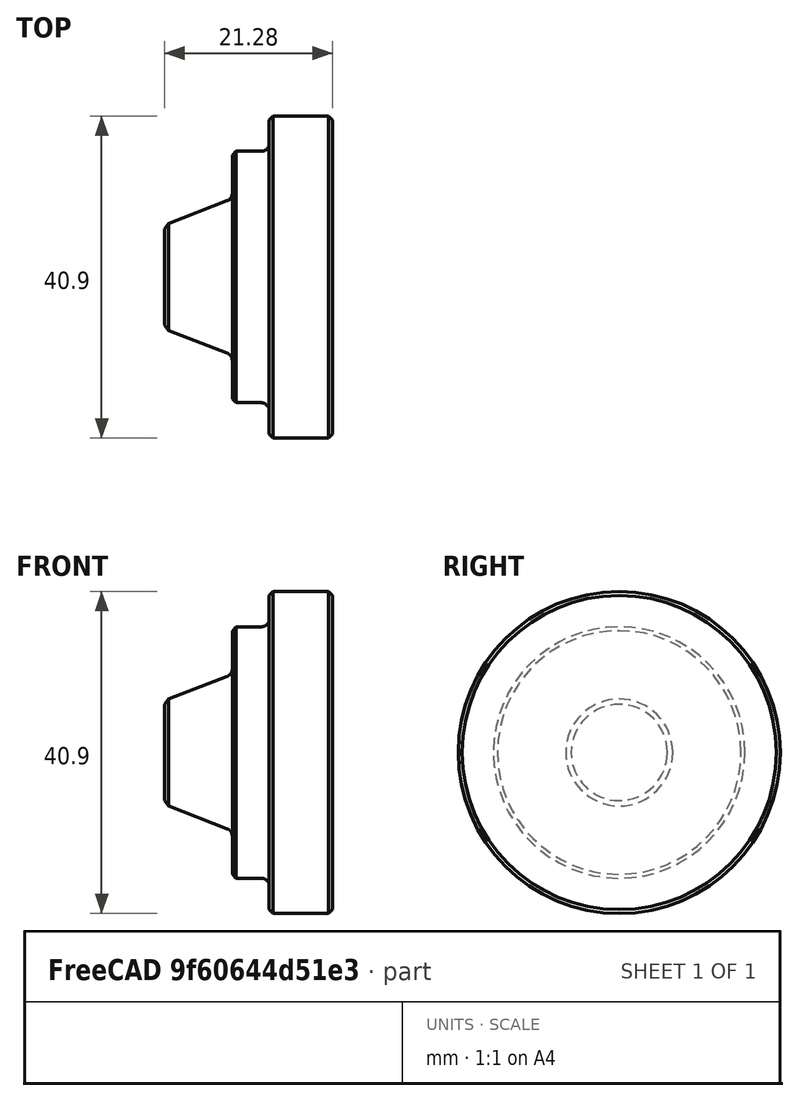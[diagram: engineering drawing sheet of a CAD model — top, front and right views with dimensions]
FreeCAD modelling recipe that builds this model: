
FCSTD DOCUMENT  (FreeCAD 0.19R24291 (Git))
Label: surface-roughness
License: All rights reserved
LicenseURL: http://en.wikipedia.org/wiki/All_rights_reserved
objects: TechDraw::DrawViewSymbol×16, TechDraw::DrawViewAnnotation×5, Sketcher::SketchObject×2, PartDesign::Revolution×2, PartDesign::Chamfer×2, PartDesign::Fillet×2, PartDesign::Body×2, TechDraw::DrawProjGroupItem×2, TechDraw::DrawSVGTemplate×1, TechDraw::DrawProjGroup×1, TechDraw::DrawViewBalloon×1, TechDraw::DrawPage×1
note: 16 computed .brp shape members not serialized (recipe doc carries the construction recipe); baked Part::Feature solids carry a one-line shape summary decoded from their .brp

FEATURE [Sketcher::SketchObject] Sketch
  FullyConstrained = true
  MapMode = 5
  Support = -> [XY_Plane]
  sketch-geometry (8):
    g0: LineSegment StartX=0 StartY=0 StartZ=0 EndX=0 EndY=6.61 EndZ=0
    g1: LineSegment StartX=0 StartY=6.61 StartZ=0 EndX=8.58 EndY=9.93 EndZ=0
    g2: LineSegment StartX=8.58 StartY=9.93 StartZ=0 EndX=8.58 EndY=15.97 EndZ=0
    g3: LineSegment StartX=8.58 StartY=15.97 StartZ=0 EndX=13.27 EndY=15.97 EndZ=0
    g4: LineSegment StartX=13.27 StartY=15.97 StartZ=0 EndX=13.27 EndY=20.45 EndZ=0
    g5: LineSegment StartX=13.27 StartY=20.45 StartZ=0 EndX=21.28 EndY=20.45 EndZ=0
    g6: LineSegment StartX=21.28 StartY=20.45 StartZ=0 EndX=21.28 EndY=0 EndZ=0
    g7: LineSegment StartX=21.28 StartY=0 StartZ=0 EndX=0 EndY=0 EndZ=0
  constraints (23):
    c: Coincident(g0,g-1)
    c: PointOnObject(g0,g-2)
    c: Coincident(g0,g1)
    c: Coincident(g1,g2)
    c: Vertical(g2)
    c: Coincident(g2,g3)
    c: Coincident(g3,g4)
    c: Vertical(g4)
    c: Coincident(g4,g5)
    c: Horizontal(g5)
    c: Coincident(g5,g6)
    c: PointOnObject(g6,g-1)
    c: Vertical(g6)
    c: Coincident(g6,g7)
    c: Coincident(g7,g0)
    c: Horizontal(g3)
    c: DistanceX(g5,g5) = 8.01
    c: DistanceY(g6,g6) = 20.45
    c: DistanceY(g0,g0) = 6.61
    c: DistanceY(g2,g2) = 6.04
    c: DistanceY(g4,g4) = 4.48
    c: DistanceX(g7,g7) = 21.28
    c: DistanceX(g3,g3) = 4.69
FEATURE [PartDesign::Revolution] Revolution
  Angle = 360
  Axis = (1,0,0)
  Base = (0,0,0)
  Profile = -> Sketch
  ReferenceAxis = -> X_Axis
  Reversed = true
FEATURE [PartDesign::Chamfer] Chamfer
  Angle = 45
  Base = -> Revolution [Edge1,Edge4,Edge7,Edge8]
  BaseFeature = -> Revolution
  ChamferType = 0
  FlipDirection = false
  Size = 0.5
  Size2 = 1
  SupportTransform = false
FEATURE [PartDesign::Fillet] Fillet
  Base = -> Chamfer [Edge5,Edge10]
  BaseFeature = -> Chamfer
  Radius = 1
  SupportTransform = false
FEATURE [PartDesign::Body] Body
  Group = -> [Sketch,Revolution,Chamfer,Fillet]
  Origin = -> Origin
  Tip = -> Fillet
FEATURE [TechDraw::DrawSVGTemplate] Template
  EditableTexts = Designed_by_Name=Designed by Name; Drawing_number=Drawing number; FC-Date=Date; FC-SC=Scale; FC-SH=Sheet; FC-Title=Title; Subtitle=Subtitle; Weight=Weight
  Height = 210
  Orientation = 1
  Width = 297
FEATURE [TechDraw::DrawProjGroupItem] ProjItem  label="Front"
  CoarseView = false
  Direction = (-1,0,0)
  Focus = 100
  HardHidden = false
  IsoCount = 0
  IsoHidden = false
  IsoVisible = false
  LockPosition = true
  Perspective = false
  Rotation = 0
  RotationVector = (0,-1,0)
  Scale = 2
  ScaleType = 2
  SeamHidden = false
  SeamVisible = true
  SmoothHidden = false
  SmoothVisible = true
  Source = -> [Body]
  Type = 0
  X = 0
  XDirection = (0,-1,0)
  Y = 0
FEATURE [TechDraw::DrawProjGroupItem] ProjItem001  label="Left"
  CoarseView = false
  Direction = (-1e-16,1,0)
  Focus = 100
  HardHidden = false
  IsoCount = 0
  IsoHidden = false
  IsoVisible = false
  LockPosition = false
  Perspective = false
  Rotation = 0
  RotationVector = (1,0,0)
  Scale = 2
  ScaleType = 2
  SeamHidden = false
  SeamVisible = true
  SmoothHidden = false
  SmoothVisible = true
  Source = -> [Body]
  Type = 1
  X = 77.18
  XDirection = (-1,-1e-16,0)
  Y = 0
FEATURE [TechDraw::DrawProjGroup] ProjGroup
  Anchor = -> ProjItem
  AutoDistribute = true
  LockPosition = false
  ProjectionType = 0
  Rotation = 0
  Scale = 2
  ScaleType = 2
  Source = -> [Body]
  Views = -> [ProjItem,ProjItem001]
  X = 86.8739
  Y = 132.576
  spacingX = 15
  spacingY = 15
FEATURE [TechDraw::DrawViewSymbol] Symbol
  LockPosition = false
  Rotation = 0
  ScaleType = 2
  Symbol = <?xml version="1.0" encoding="UTF-8" standalone="no"?>\n<!-- Created with Inkscape (http://www.inkscape.org/) -->\n\n<svg\n   width="24.9319mm"\n   height="10.867571mm"\n   viewBox="0 0 24.9319 10.867571"\n   version="1.1"\n   id="svg5"\n   inkscape:version="1.1.1 (3bf5ae0d25, 2021-09-20)"\n   sodipodi:docname="roughness.svg"\n   xmlns:inkscape="http://www.inkscape.org/namespaces/inkscape"\n   xmlns:sodipodi="http://sodipodi.sourceforge.net/DTD/sodipodi-0.dtd"\n   xmlns="http://www.w3.org/2000/svg"\n   xmlns:svg="http://www.w3.org/2000/svg">\n  <sodipodi:namedview\n     id="namedview7"\n     pagecolor="#ffffff"\n     bordercolor="#999999"\n     borderopacity="1"\n     inkscape:pageshadow="0"\n     inkscape:pageopacity="0"\n     inkscape:pagecheckerboard="0"\n     inkscape:document-units="mm"\n     showgrid="false"\n     inkscape:zoom="3.1108586"\n     inkscape:cx="78.113483"\n     inkscape:cy="5.6254566"\n     inkscape:window-width="1600"\n     inkscape:window-height="1137"\n     inkscape:window-x="-8"\n     inkscape:window-y="-8"\n     inkscape:window-maximized="1"\n     inkscape:current-layer="layer1"\n     showborder="true"\n     fit-margin-top="0"\n     fit-margin-left="0"\n     fit-margin-right="0"\n     fit-margin-bottom="0" />\n  <defs\n     id="defs2" />\n  <g\n     inkscape:label="Ebene 1"\n     inkscape:groupmode="layer"\n     id="layer1"\n     transform="translate(-13.037144,-40.097097)">\n    <path\n       style="fill:none;stroke:#000000;stroke-width:0.135895px;stroke-linecap:butt;stroke-linejoin:miter;stroke-opacity:1"\n       d="m 13.155737,45.756607 2.97052,5.067357 2.621047,-5.067357 z"\n       id="path42" />\n    <path\n       style="fill:none;stroke:#000000;stroke-width:0.135895px;stroke-linecap:butt;stroke-linejoin:miter;stroke-opacity:1"\n       d="m 18.747304,45.756607 2.970519,-5.41683 16.25049,-0.174736"\n       id="path44" />\n  </g>\n</svg>
  X = 203.662
  Y = 173.18
FEATURE [TechDraw::DrawViewAnnotation] Annotation
  Font = osifont
  LineSpace = 80
  LockPosition = false
  MaxWidth = -1
  Rotation = 0
  ScaleType = 0
  Text = Ra 6,3
  TextSize = 5
  TextStyle = 0
  X = 207.602
  Y = 173.223
FEATURE [TechDraw::DrawViewSymbol] Symbol001
  LockPosition = false
  Rotation = 0
  ScaleType = 2
  Symbol = <?xml version="1.0" encoding="UTF-8" standalone="no"?>\n<!-- Created with Inkscape (http://www.inkscape.org/) -->\n\n<svg\n   width="8.6807499mm"\n   height="10.655431mm"\n   viewBox="0 0 8.6807499 10.655431"\n   version="1.1"\n   id="svg5"\n   inkscape:version="1.1.1 (3bf5ae0d25, 2021-09-20)"\n   sodipodi:docname="roughness-1-1.svg"\n   xmlns:inkscape="http://www.inkscape.org/namespaces/inkscape"\n   xmlns:sodipodi="http://sodipodi.sourceforge.net/DTD/sodipodi-0.dtd"\n   xmlns="http://www.w3.org/2000/svg"\n   xmlns:svg="http://www.w3.org/2000/svg">\n  <sodipodi:namedview\n     id="namedview7"\n     pagecolor="#ffffff"\n     bordercolor="#999999"\n     borderopacity="1"\n     inkscape:pageshadow="0"\n     inkscape:pageopacity="0"\n     inkscape:pagecheckerboard="0"\n     inkscape:document-units="mm"\n     showgrid="false"\n     inkscape:zoom="8.7988368"\n     inkscape:cx="19.491213"\n     inkscape:cy="16.877231"\n     inkscape:window-width="1600"\n     inkscape:window-height="1137"\n     inkscape:window-x="-8"\n     inkscape:window-y="-8"\n     inkscape:window-maximized="1"\n     inkscape:current-layer="layer2"\n     showborder="true"\n     fit-margin-top="0"\n     fit-margin-left="0"\n     fit-margin-right="0"\n     fit-margin-bottom="0" />\n  <defs\n     id="defs2" />\n  <g\n     inkscape:groupmode="layer"\n     id="layer2"\n     inkscape:label="Ebene 2"\n     style="display:inline"\n     transform="translate(-0.05992954,-0.21068)">\n    <path\n       style="fill:none;stroke:#000000;stroke-width:0.136;stroke-linecap:butt;stroke-linejoin:miter;stroke-miterlimit:4;stroke-dasharray:none;stroke-opacity:1"\n       d="M 0.118593,5.6595099 3.089113,10.726867 8.680679,0.24268"\n       id="path1391" />\n  </g>\n</svg>
  X = 203.172
  Y = 151.04
FEATURE [TechDraw::DrawViewSymbol] Symbol002
  LockPosition = false
  Rotation = 0
  ScaleType = 2
  Symbol = <?xml version="1.0" encoding="UTF-8" standalone="no"?>\n<!-- Created with Inkscape (http://www.inkscape.org/) -->\n\n<svg\n   width="8.7402563mm"\n   height="10.657563mm"\n   viewBox="0 0 8.7402563 10.657563"\n   version="1.1"\n   id="svg5"\n   inkscape:version="1.1.1 (3bf5ae0d25, 2021-09-20)"\n   sodipodi:docname="roughness-1-2.svg"\n   xmlns:inkscape="http://www.inkscape.org/namespaces/inkscape"\n   xmlns:sodipodi="http://sodipodi.sourceforge.net/DTD/sodipodi-0.dtd"\n   xmlns="http://www.w3.org/2000/svg"\n   xmlns:svg="http://www.w3.org/2000/svg">\n  <sodipodi:namedview\n     id="namedview7"\n     pagecolor="#ffffff"\n     bordercolor="#999999"\n     borderopacity="1"\n     inkscape:pageshadow="0"\n     inkscape:pageopacity="0"\n     inkscape:pagecheckerboard="0"\n     inkscape:document-units="mm"\n     showgrid="false"\n     inkscape:zoom="6.2217172"\n     inkscape:cx="43.63747"\n     inkscape:cy="16.153097"\n     inkscape:window-width="1600"\n     inkscape:window-height="1137"\n     inkscape:window-x="-8"\n     inkscape:window-y="-8"\n     inkscape:window-maximized="1"\n     inkscape:current-layer="layer1"\n     showborder="true"\n     fit-margin-top="0"\n     fit-margin-left="0"\n     fit-margin-right="0"\n     fit-margin-bottom="0" />\n  <defs\n     id="defs2" />\n  <g\n     inkscape:label="Ebene 1"\n     inkscape:groupmode="layer"\n     id="layer1"\n     transform="translate(-13.037144,-40.307106)">\n    <path\n       style="fill:none;stroke:#000000;stroke-width:0.135895px;stroke-linecap:butt;stroke-linejoin:miter;stroke-opacity:1"\n       d="m 13.155737,45.756607 2.97052,5.067357 2.621047,-5.067357 z"\n       id="path42" />\n    <path\n       style="fill:none;stroke:#000000;stroke-width:0.135895px;stroke-linecap:butt;stroke-linejoin:miter;stroke-opacity:1"\n       d="m 18.747304,45.756607 2.970519,-5.41683"\n       id="path44"\n       sodipodi:nodetypes="cc" />\n  </g>\n</svg>
  X = 227.151
  Y = 151.519
FEATURE [TechDraw::DrawViewSymbol] Symbol003
  LockPosition = false
  Rotation = 0
  ScaleType = 2
  Symbol = <?xml version="1.0" encoding="UTF-8" standalone="no"?>\n<!-- Created with Inkscape (http://www.inkscape.org/) -->\n\n<svg\n   width="8.6807499mm"\n   height="10.655431mm"\n   viewBox="0 0 8.6807499 10.655431"\n   version="1.1"\n   id="svg5"\n   inkscape:version="1.1.1 (3bf5ae0d25, 2021-09-20)"\n   sodipodi:docname="roughness-1-3.svg"\n   xmlns:inkscape="http://www.inkscape.org/namespaces/inkscape"\n   xmlns:sodipodi="http://sodipodi.sourceforge.net/DTD/sodipodi-0.dtd"\n   xmlns="http://www.w3.org/2000/svg"\n   xmlns:svg="http://www.w3.org/2000/svg">\n  <sodipodi:namedview\n     id="namedview7"\n     pagecolor="#ffffff"\n     bordercolor="#999999"\n     borderopacity="1"\n     inkscape:pageshadow="0"\n     inkscape:pageopacity="0"\n     inkscape:pagecheckerboard="0"\n     inkscape:document-units="mm"\n     showgrid="false"\n     inkscape:zoom="4.3994184"\n     inkscape:cx="-19.66169"\n     inkscape:cy="7.3873401"\n     inkscape:window-width="1600"\n     inkscape:window-height="1137"\n     inkscape:window-x="-8"\n     inkscape:window-y="-8"\n     inkscape:window-maximized="1"\n     inkscape:current-layer="layer2"\n     showborder="true"\n     fit-margin-top="0"\n     fit-margin-left="0"\n     fit-margin-right="0"\n     fit-margin-bottom="0" />\n  <defs\n     id="defs2" />\n  <g\n     inkscape:groupmode="layer"\n     id="layer2"\n     inkscape:label="Ebene 2"\n     style="display:inline"\n     transform="translate(-0.05992954,-0.21068)">\n    <path\n       style="fill:none;stroke:#000000;stroke-width:0.136;stroke-linecap:butt;stroke-linejoin:miter;stroke-miterlimit:4;stroke-dasharray:none;stroke-opacity:1"\n       d="M 0.118593,5.6595099 3.089113,10.726867 8.680679,0.24268"\n       id="path1391" />\n    <circle\n       style="fill:none;stroke:#000000;stroke-width:0.143064"\n       id="path844"\n       cx="2.9923141"\n       cy="7.0797095"\n       r="1.7555785" />\n  </g>\n</svg>
  X = 250.411
  Y = 151.759
FEATURE [TechDraw::DrawViewSymbol] Symbol004
  LockPosition = false
  Rotation = 0
  ScaleType = 2
  Symbol = <?xml version="1.0" encoding="UTF-8" standalone="no"?>\n<!-- Created with Inkscape (http://www.inkscape.org/) -->\n\n<svg\n   width="24.9319mm"\n   height="10.867571mm"\n   viewBox="0 0 24.9319 10.867571"\n   version="1.1"\n   id="svg5"\n   inkscape:version="1.1.1 (3bf5ae0d25, 2021-09-20)"\n   sodipodi:docname="roughness-1-4.svg"\n   xmlns:inkscape="http://www.inkscape.org/namespaces/inkscape"\n   xmlns:sodipodi="http://sodipodi.sourceforge.net/DTD/sodipodi-0.dtd"\n   xmlns="http://www.w3.org/2000/svg"\n   xmlns:svg="http://www.w3.org/2000/svg">\n  <sodipodi:namedview\n     id="namedview7"\n     pagecolor="#ffffff"\n     bordercolor="#999999"\n     borderopacity="1"\n     inkscape:pageshadow="0"\n     inkscape:pageopacity="0"\n     inkscape:pagecheckerboard="0"\n     inkscape:document-units="mm"\n     showgrid="false"\n     inkscape:zoom="8.7988368"\n     inkscape:cx="49.60883"\n     inkscape:cy="27.219507"\n     inkscape:window-width="1600"\n     inkscape:window-height="1137"\n     inkscape:window-x="-8"\n     inkscape:window-y="-8"\n     inkscape:window-maximized="1"\n     inkscape:current-layer="layer2"\n     showborder="true"\n     fit-margin-top="0"\n     fit-margin-left="0"\n     fit-margin-right="0"\n     fit-margin-bottom="0" />\n  <defs\n     id="defs2" />\n  <g\n     inkscape:groupmode="layer"\n     id="layer2"\n     inkscape:label="Ebene 2">\n    <path\n       style="fill:none;stroke:#000000;stroke-width:0.136;stroke-linecap:butt;stroke-linejoin:miter;stroke-opacity:1;stroke-miterlimit:4;stroke-dasharray:none"\n       d="M 0.118593,5.6595099 3.089113,10.726867 8.680679,0.24268 24.931169,0.067944"\n       id="path857" />\n  </g>\n</svg>
  X = 203.412
  Y = 132.816
FEATURE [TechDraw::DrawViewSymbol] Symbol005
  LockPosition = false
  Rotation = 0
  ScaleType = 2
  Symbol = <?xml version="1.0" encoding="UTF-8" standalone="no"?>\n<!-- Created with Inkscape (http://www.inkscape.org/) -->\n\n<svg\n   width="24.871971mm"\n   height="12.704021mm"\n   viewBox="0 0 24.871971 12.704021"\n   version="1.1"\n   id="svg5"\n   inkscape:version="1.1.1 (3bf5ae0d25, 2021-09-20)"\n   sodipodi:docname="roughness-1-5.svg"\n   xmlns:inkscape="http://www.inkscape.org/namespaces/inkscape"\n   xmlns:sodipodi="http://sodipodi.sourceforge.net/DTD/sodipodi-0.dtd"\n   xmlns="http://www.w3.org/2000/svg"\n   xmlns:svg="http://www.w3.org/2000/svg">\n  <sodipodi:namedview\n     id="namedview7"\n     pagecolor="#ffffff"\n     bordercolor="#999999"\n     borderopacity="1"\n     inkscape:pageshadow="0"\n     inkscape:pageopacity="0"\n     inkscape:pagecheckerboard="0"\n     inkscape:document-units="mm"\n     showgrid="false"\n     inkscape:zoom="4.3994184"\n     inkscape:cx="40.800848"\n     inkscape:cy="43.073875"\n     inkscape:window-width="1600"\n     inkscape:window-height="1137"\n     inkscape:window-x="-8"\n     inkscape:window-y="-8"\n     inkscape:window-maximized="1"\n     inkscape:current-layer="layer2"\n     showborder="true"\n     fit-margin-top="0"\n     fit-margin-left="0"\n     fit-margin-right="0"\n     fit-margin-bottom="0" />\n  <defs\n     id="defs2" />\n  <g\n     inkscape:groupmode="layer"\n     id="layer2"\n     inkscape:label="Ebene 2"\n     transform="translate(-0.05992954,1.8379097)">\n    <path\n       style="fill:none;stroke:#000000;stroke-width:0.136;stroke-linecap:butt;stroke-linejoin:miter;stroke-miterlimit:4;stroke-dasharray:none;stroke-opacity:1"\n       d="M 0.118593,5.6595099 3.089113,10.726867 8.680679,0.24268 24.931169,0.067944"\n       id="path857" />\n    <circle\n       style="fill:none;stroke:#000000;stroke-width:0.136"\n       id="path844"\n       cx="8.6806784"\n       cy="0.24268"\n       r="2.0125897" />\n  </g>\n</svg>
  X = 228.59
  Y = 132.096
FEATURE [TechDraw::DrawViewSymbol] Symbol006
  LockPosition = false
  Rotation = 0
  ScaleType = 2
  Symbol = <?xml version="1.0" encoding="UTF-8" standalone="no"?>\n<!-- Created with Inkscape (http://www.inkscape.org/) -->\n\n<svg\n   width="24.9319mm"\n   height="10.867571mm"\n   viewBox="0 0 24.9319 10.867571"\n   version="1.1"\n   id="svg5"\n   inkscape:version="1.1.1 (3bf5ae0d25, 2021-09-20)"\n   sodipodi:docname="roughness.svg"\n   xmlns:inkscape="http://www.inkscape.org/namespaces/inkscape"\n   xmlns:sodipodi="http://sodipodi.sourceforge.net/DTD/sodipodi-0.dtd"\n   xmlns="http://www.w3.org/2000/svg"\n   xmlns:svg="http://www.w3.org/2000/svg">\n  <sodipodi:namedview\n     id="namedview7"\n     pagecolor="#ffffff"\n     bordercolor="#999999"\n     borderopacity="1"\n     inkscape:pageshadow="0"\n     inkscape:pageopacity="0"\n     inkscape:pagecheckerboard="0"\n     inkscape:document-units="mm"\n     showgrid="false"\n     inkscape:zoom="3.1108586"\n     inkscape:cx="78.113483"\n     inkscape:cy="5.6254566"\n     inkscape:window-width="1600"\n     inkscape:window-height="1137"\n     inkscape:window-x="-8"\n     inkscape:window-y="-8"\n     inkscape:window-maximized="1"\n     inkscape:current-layer="layer1"\n     showborder="true"\n     fit-margin-top="0"\n     fit-margin-left="0"\n     fit-margin-right="0"\n     fit-margin-bottom="0" />\n  <defs\n     id="defs2" />\n  <g\n     inkscape:label="Ebene 1"\n     inkscape:groupmode="layer"\n     id="layer1"\n     transform="translate(-13.037144,-40.097097)">\n    <path\n       style="fill:none;stroke:#000000;stroke-width:0.135895px;stroke-linecap:butt;stroke-linejoin:miter;stroke-opacity:1"\n       d="m 13.155737,45.756607 2.97052,5.067357 2.621047,-5.067357 z"\n       id="path42" />\n    <path\n       style="fill:none;stroke:#000000;stroke-width:0.135895px;stroke-linecap:butt;stroke-linejoin:miter;stroke-opacity:1"\n       d="m 18.747304,45.756607 2.970519,-5.41683 16.25049,-0.174736"\n       id="path44" />\n  </g>\n</svg>
  X = 253.288
  Y = 132.336
FEATURE [Sketcher::SketchObject] Sketch001
  FullyConstrained = true
  MapMode = 5
  Support = -> [XY_Plane001]
  sketch-geometry (8):
    g0: LineSegment StartX=0 StartY=0 StartZ=0 EndX=0 EndY=6.61 EndZ=0
    g1: LineSegment StartX=0 StartY=6.61 StartZ=0 EndX=8.58 EndY=9.93 EndZ=0
    g2: LineSegment StartX=8.58 StartY=9.93 StartZ=0 EndX=8.58 EndY=15.97 EndZ=0
    g3: LineSegment StartX=8.58 StartY=15.97 StartZ=0 EndX=13.27 EndY=15.97 EndZ=0
    g4: LineSegment StartX=13.27 StartY=15.97 StartZ=0 EndX=13.27 EndY=20.45 EndZ=0
    g5: LineSegment StartX=13.27 StartY=20.45 StartZ=0 EndX=21.28 EndY=20.45 EndZ=0
    g6: LineSegment StartX=21.28 StartY=20.45 StartZ=0 EndX=21.28 EndY=0 EndZ=0
    g7: LineSegment StartX=21.28 StartY=0 StartZ=0 EndX=0 EndY=0 EndZ=0
  constraints (23):
    c: Coincident(g0,g-1)
    c: PointOnObject(g0,g-2)
    c: Coincident(g0,g1)
    c: Coincident(g1,g2)
    c: Vertical(g2)
    c: Coincident(g2,g3)
    c: Coincident(g3,g4)
    c: Vertical(g4)
    c: Coincident(g4,g5)
    c: Horizontal(g5)
    c: Coincident(g5,g6)
    c: PointOnObject(g6,g-1)
    c: Vertical(g6)
    c: Coincident(g6,g7)
    c: Coincident(g7,g0)
    c: Horizontal(g3)
    c: DistanceX(g5,g5) = 8.01
    c: DistanceY(g6,g6) = 20.45
    c: DistanceY(g0,g0) = 6.61
    c: DistanceY(g2,g2) = 6.04
    c: DistanceY(g4,g4) = 4.48
    c: DistanceX(g7,g7) = 21.28
    c: DistanceX(g3,g3) = 4.69
FEATURE [PartDesign::Revolution] Revolution001
  Angle = 360
  Axis = (1,0,0)
  Base = (0,0,0)
  Profile = -> Sketch001
  ReferenceAxis = -> X_Axis001
  Reversed = true
FEATURE [PartDesign::Chamfer] Chamfer001
  Angle = 45
  Base = -> Revolution001 [Edge1,Edge4,Edge7,Edge8]
  BaseFeature = -> Revolution001
  ChamferType = 0
  FlipDirection = false
  Size = 0.5
  Size2 = 1
  SupportTransform = false
FEATURE [PartDesign::Fillet] Fillet001
  Base = -> Chamfer001 [Edge5,Edge10]
  BaseFeature = -> Chamfer001
  Radius = 1
  SupportTransform = false
FEATURE [PartDesign::Body] Body001
  Group = -> [Sketch001,Revolution001,Chamfer001,Fillet001]
  Origin = -> Origin001
  Tip = -> Fillet001
FEATURE [TechDraw::DrawViewSymbol] Symbol007
  LockPosition = false
  Rotation = 0
  ScaleType = 2
  Symbol = <?xml version="1.0" encoding="UTF-8" standalone="no"?>\n<!-- Created with Inkscape (http://www.inkscape.org/) -->\n\n<svg\n   width="5.5755901mm"\n   height="5.7456932mm"\n   viewBox="0 0 5.5755901 5.7456932"\n   version="1.1"\n   id="svg5"\n   inkscape:version="1.1.1 (3bf5ae0d25, 2021-09-20)"\n   sodipodi:docname="edge.svg"\n   xmlns:inkscape="http://www.inkscape.org/namespaces/inkscape"\n   xmlns:sodipodi="http://sodipodi.sourceforge.net/DTD/sodipodi-0.dtd"\n   xmlns="http://www.w3.org/2000/svg"\n   xmlns:svg="http://www.w3.org/2000/svg">\n  <sodipodi:namedview\n     id="namedview7"\n     pagecolor="#ffffff"\n     bordercolor="#999999"\n     borderopacity="1"\n     inkscape:pageshadow="0"\n     inkscape:pageopacity="0"\n     inkscape:pagecheckerboard="0"\n     inkscape:document-units="mm"\n     showgrid="false"\n     inkscape:zoom="3.1108586"\n     inkscape:cx="9.6436399"\n     inkscape:cy="16.554915"\n     inkscape:window-width="1600"\n     inkscape:window-height="1137"\n     inkscape:window-x="-8"\n     inkscape:window-y="-8"\n     inkscape:window-maximized="1"\n     inkscape:current-layer="layer1"\n     fit-margin-top="0"\n     fit-margin-left="0"\n     fit-margin-right="0"\n     fit-margin-bottom="0" />\n  <defs\n     id="defs2" />\n  <g\n     inkscape:label="Layer 1"\n     inkscape:groupmode="layer"\n     id="layer1"\n     transform="translate(-6.501729,-6.6340204)">\n    <path\n       style="fill:none;stroke:#000000;stroke-width:0.264583px;stroke-linecap:butt;stroke-linejoin:miter;stroke-opacity:1"\n       d="M 6.6340205,6.6340204 V 12.247422 H 12.077319"\n       id="path876" />\n  </g>\n</svg>
  X = 181.077
  Y = 187.959
FEATURE [TechDraw::DrawViewBalloon] Balloon001
  BubbleShape = 1
  EndType = 0
  EndTypeScale = 1
  KinkLength = 5
  LockPosition = false
  OriginX = 1.4381
  OriginY = 15.9716
  Rotation = 0
  ScaleType = 0
  ShapeScale = 1
  SourceView = -> ProjItem001
  TextWrapLen = -1
  X = 11.4381
  Y = 25.9716
FEATURE [TechDraw::DrawViewAnnotation] Annotation001
  Font = osifont
  LineSpace = 80
  LockPosition = false
  MaxWidth = -1
  Rotation = 0
  ScaleType = 0
  Text = -0,1 | -0,3
  TextSize = 3.5
  TextStyle = 0
  X = 182.513
  Y = 189.136
FEATURE [TechDraw::DrawViewSymbol] Symbol008
  LockPosition = false
  Rotation = 0
  ScaleType = 2
  Symbol = <blob: 2108 chars omitted>
  X = 211.52
  Y = 74.24
FEATURE [TechDraw::DrawViewAnnotation] Annotation002
  Font = osifont
  LineSpace = 80
  LockPosition = false
  MaxWidth = -1
  Rotation = 0
  ScaleType = 0
  Text = -0,5
  TextSize = 3.5
  TextStyle = 0
  X = 215.012
  Y = 76.2385
FEATURE [TechDraw::DrawViewSymbol] Symbol009
  LockPosition = false
  Rotation = 0
  ScaleType = 2
  Symbol = <blob: 2323 chars omitted>
  X = 231.987
  Y = 72.7255
FEATURE [TechDraw::DrawViewSymbol] Symbol010
  LockPosition = false
  Rotation = 0
  ScaleType = 2
  Symbol = <blob: 2336 chars omitted>
  X = 254.12
  Y = 73.1044
FEATURE [TechDraw::DrawViewSymbol] Symbol011
  LockPosition = false
  Rotation = 0
  ScaleType = 2
  Symbol = <?xml version="1.0" encoding="UTF-8" standalone="no"?>\n<!-- Created with Inkscape (http://www.inkscape.org/) -->\n\n<svg\n   width="5.5755901mm"\n   height="5.7456932mm"\n   viewBox="0 0 5.5755901 5.7456932"\n   version="1.1"\n   id="svg5"\n   inkscape:version="1.1.1 (3bf5ae0d25, 2021-09-20)"\n   sodipodi:docname="edge.svg"\n   xmlns:inkscape="http://www.inkscape.org/namespaces/inkscape"\n   xmlns:sodipodi="http://sodipodi.sourceforge.net/DTD/sodipodi-0.dtd"\n   xmlns="http://www.w3.org/2000/svg"\n   xmlns:svg="http://www.w3.org/2000/svg">\n  <sodipodi:namedview\n     id="namedview7"\n     pagecolor="#ffffff"\n     bordercolor="#999999"\n     borderopacity="1"\n     inkscape:pageshadow="0"\n     inkscape:pageopacity="0"\n     inkscape:pagecheckerboard="0"\n     inkscape:document-units="mm"\n     showgrid="false"\n     inkscape:zoom="3.1108586"\n     inkscape:cx="9.6436399"\n     inkscape:cy="16.554915"\n     inkscape:window-width="1600"\n     inkscape:window-height="1137"\n     inkscape:window-x="-8"\n     inkscape:window-y="-8"\n     inkscape:window-maximized="1"\n     inkscape:current-layer="layer1"\n     fit-margin-top="0"\n     fit-margin-left="0"\n     fit-margin-right="0"\n     fit-margin-bottom="0" />\n  <defs\n     id="defs2" />\n  <g\n     inkscape:label="Layer 1"\n     inkscape:groupmode="layer"\n     id="layer1"\n     transform="translate(-6.501729,-6.6340204)">\n    <path\n       style="fill:none;stroke:#000000;stroke-width:0.264583px;stroke-linecap:butt;stroke-linejoin:miter;stroke-opacity:1"\n       d="M 6.6340205,6.6340204 V 12.247422 H 12.077319"\n       id="path876" />\n  </g>\n</svg>
  X = 181.071
  Y = 188.327
FEATURE [TechDraw::DrawViewAnnotation] Annotation003
  Font = osifont
  LineSpace = 80
  LockPosition = false
  MaxWidth = -1
  Rotation = 0
  ScaleType = 0
  Text = -0,1 | -0,3
  TextSize = 3.5
  TextStyle = 0
  X = 236.405
  Y = 76.8701
FEATURE [TechDraw::DrawViewAnnotation] Annotation004
  Font = osifont
  LineSpace = 80
  LockPosition = false
  MaxWidth = -1
  Rotation = 0
  ScaleType = 0
  Text = +0,3
  TextSize = 3.5
  TextStyle = 0
  X = 256.466
  Y = 80.5384
FEATURE [TechDraw::DrawViewSymbol] Symbol012
  EditableTexts = Ra 12,5
  LockPosition = false
  Rotation = 0
  ScaleType = 2
  Symbol = <blob: 2016 chars omitted>
  X = 246.157
  Y = 153.823
FEATURE [TechDraw::DrawViewSymbol] Symbol013
  EditableTexts = Ra 6,3
  LockPosition = false
  Rotation = 0
  ScaleType = 2
  Symbol = <blob: 2038 chars omitted>
  X = 220.104
  Y = 153.624
FEATURE [TechDraw::DrawViewSymbol] Symbol014
  EditableTexts = Ra 3,2
  LockPosition = false
  Rotation = 0
  ScaleType = 2
  Symbol = <blob: 2038 chars omitted>
  X = 220.104
  Y = 134.308
FEATURE [TechDraw::DrawViewSymbol] Symbol015
  EditableTexts = Ra 1,6
  LockPosition = false
  Rotation = 0
  ScaleType = 2
  Symbol = <blob: 2038 chars omitted>
  X = 246.248
  Y = 133.975
FEATURE [TechDraw::DrawPage] Page
  KeepUpdated = true
  NextBalloonIndex = 7
  ProjectionType = 0
  Template = -> Template
  Views = -> [ProjGroup,Symbol,Annotation,Symbol001,Symbol002,Symbol003,Symbol004,Symbol005,Symbol006,Symbol007,Balloon001,Annotation001,Symbol008,Annotation002,Symbol009,Symbol010,Symbol011,Annotation003,Annotation004,Symbol012,Symbol013,Symbol014,Symbol015]
